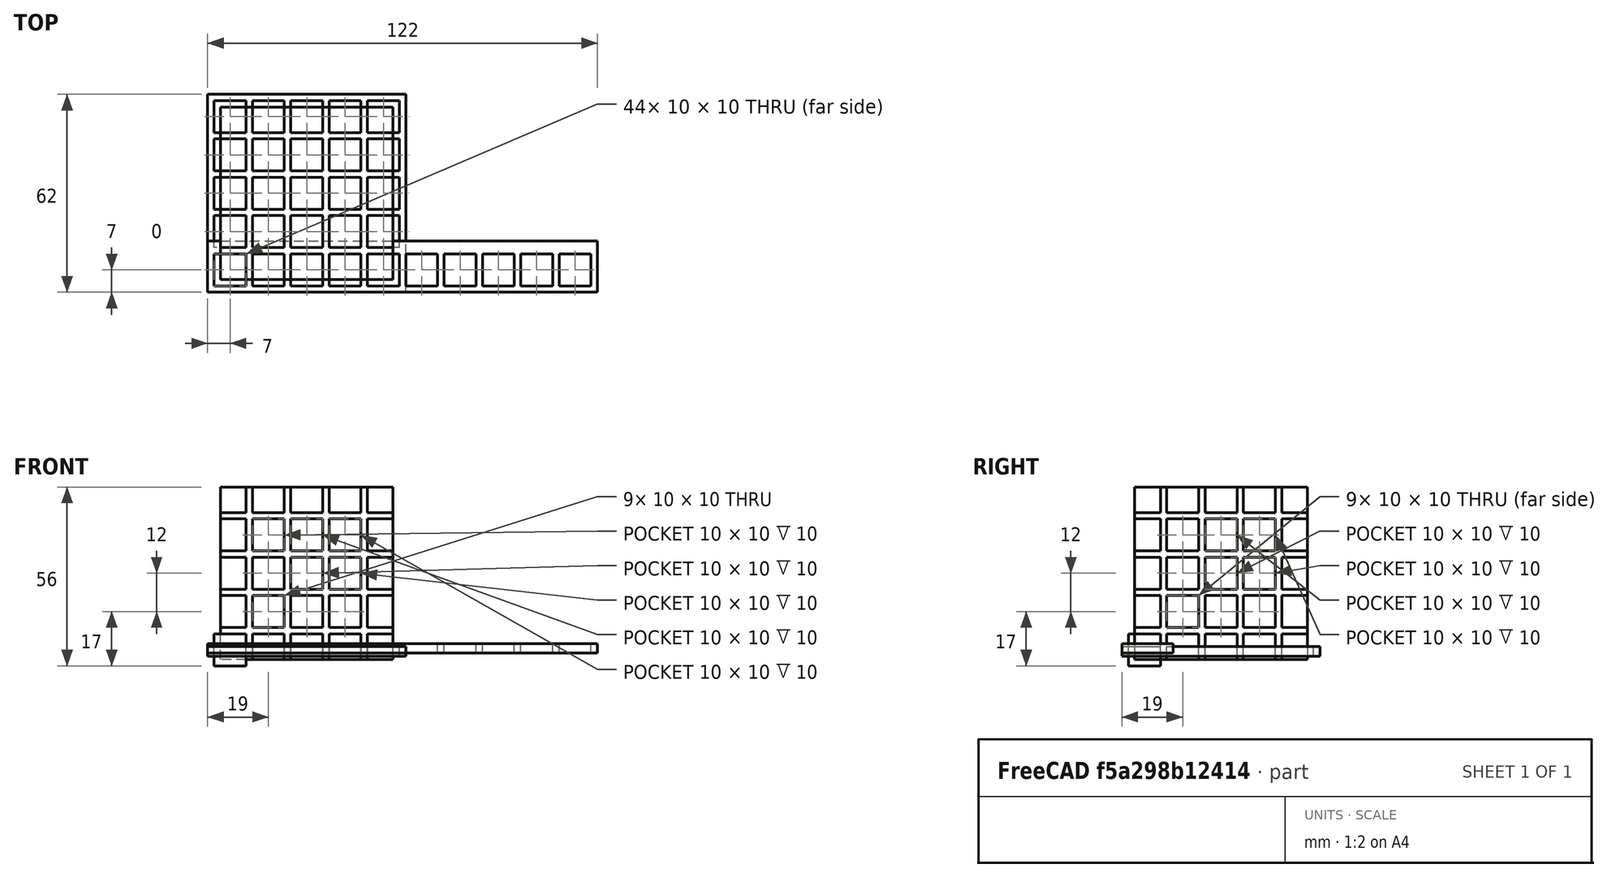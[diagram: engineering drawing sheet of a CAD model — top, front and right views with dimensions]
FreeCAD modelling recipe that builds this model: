
FCSTD DOCUMENT  (FreeCAD 1.0R39319 (Git))
Label: ojt1_t10p01_array
License: All rights reserved
LicenseURL: https://en.wikipedia.org/wiki/All_rights_reserved
objects: Part::Box×6, Part::FeaturePython×3, Part::Cut×3, PartDesign::Body×1
note: 10 computed .brp shape members not serialized (recipe doc carries the construction recipe); baked Part::Feature solids carry a one-line shape summary decoded from their .brp

FEATURE [PartDesign::Body] Body  label="master box"
  AllowCompound = false
  Origin = -> Origin
FEATURE [Part::Box] Box  label="Cub"
  AttacherType = Attacher::AttachEngine3D
  Height = 10
  Length = 10
  Width = 10
FEATURE [Part::FeaturePython] Array  # Draft array (typed FeaturePython)
  AlwaysSyncPlacement = false
  Angle = 360
  ArrayType = 0
  Axis = (0,0,1)
  Base = -> Box
  Center = (0,0,0)
  Count = 10
  ExpandArray = false
  Fuse = false
  IntervalAxis = (0,0,0)
  IntervalX = (12,0,0)
  IntervalY = (0,100,0)
  IntervalZ = (0,0,100)
  NumberCircles = 3
  NumberPolar = 5
  NumberX = 10
  NumberY = 1
  NumberZ = 1
  PlacementList = 10 placements: arithmetic series from (0,0,0) step (12,0,0) to (108,0,0)
  RadialDistance = 50
  ScaleList = (10) [(1,1,1),(1,1,1),(1,1,1),(1,1,1),(1,1,1),(1,1,1),(1,1,1),(1,1,1),(1,1,1),(1,1,1)]
  Symmetry = 1
  TangentialDistance = 25
FEATURE [Part::Box] Box001  label="Cub001"
  AttacherType = Attacher::AttachEngine3D
  Height = 3
  Length = 122
  Placement = pos=(-2,-2,4) rot=(0,0,1;0rad)
  Width = 16
FEATURE [Part::Cut] Cut
  Base = -> Box001
  Tool = -> Array
FEATURE [Part::Box] Box002  label="Cub002"
  AttacherType = Attacher::AttachEngine3D
  Height = 10
  Length = 10
  Width = 10
FEATURE [Part::FeaturePython] Array001  # Draft array (typed FeaturePython)
  AlwaysSyncPlacement = false
  Angle = 360
  ArrayType = 0
  Axis = (0,0,1)
  Base = -> Box002
  Center = (0,0,0)
  Count = 25
  ExpandArray = false
  Fuse = false
  IntervalAxis = (0,0,0)
  IntervalX = (12,0,0)
  IntervalY = (0,12,0)
  IntervalZ = (0,0,100)
  NumberCircles = 3
  NumberPolar = 5
  NumberX = 5
  NumberY = 5
  NumberZ = 1
  PlacementList = 25 placements: [(0,0,0),(0,12,0),(0,24,0),(0,36,0),(0,48,0),(12,0,0),(12,12,0),(12,24,0),(12,36,0),(12,48,0),(24,0,0),(24,12,0),(24,24,0),(24,36,0),(24,48,0),(36,0,0),(36,12,0),(36,24,0),(36,36,0),(36,48,0),(48,0,0),(48,12,0),(48,24,0),(48,36,0),(48,48,0)]
  RadialDistance = 50
  ScaleList = (25) [(1,1,1),(1,1,1),(1,1,1),(1,1,1),(1,1,1),(1,1,1),(1,1,1),(1,1,1),(1,1,1),(1,1,1),(1,1,1),(1,1,1),(1,1,1),(1,1,1),(1,1,1),(1,1,1),(1,1,1),(1,1,1),+7 more]
  Symmetry = 1
  TangentialDistance = 25
FEATURE [Part::Box] Box003  label="Cub003"
  AttacherType = Attacher::AttachEngine3D
  Height = 3
  Length = 62
  Placement = pos=(-2,-2,3) rot=(0,0,1;0rad)
  Width = 62
FEATURE [Part::Cut] Cut001
  Base = -> Box003
  Tool = -> Array001
FEATURE [Part::Box] Box004  label="Cub004"
  AttacherType = Attacher::AttachEngine3D
  Height = 10
  Length = 10
  Width = 10
FEATURE [Part::FeaturePython] Array002  # Draft array (typed FeaturePython)
  AlwaysSyncPlacement = false
  Angle = 360
  ArrayType = 0
  Axis = (0,0,1)
  Base = -> Box004
  Center = (0,0,0)
  Count = 125
  ExpandArray = false
  Fuse = false
  IntervalAxis = (0,0,0)
  IntervalX = (12,0,0)
  IntervalY = (0,12,0)
  IntervalZ = (0,0,12)
  NumberCircles = 3
  NumberPolar = 5
  NumberX = 5
  NumberY = 5
  NumberZ = 5
  PlacementList = 125 placements: [(0,0,0),(0,0,12),(0,0,24),(0,0,36),(0,0,48),(0,12,0),(0,12,12),(0,12,24),(0,12,36),(0,12,48),(0,24,0),(0,24,12),(0,24,24),(0,24,36),(0,24,48),(0,36,0),(0,36,12),(0,36,24),(0,36,36),(0,36,48),(0,48,0),(0,48,12),(0,48,24),(0,48,36),(0,48,48),(12,0,0),(12,0,12),(12,0,24),(12,0,36),(12,0,48),(12,12,0),(12,12,12),(12,12,24),(12,12,36),(12,12,48),(12,24,0),(12,24,12),(12,24,24),(12,24,36),(12,24,48),+85 more]
  RadialDistance = 50
  Symmetry = 1
  TangentialDistance = 25
FEATURE [Part::Box] Box005  label="Cub005"
  AttacherType = Attacher::AttachEngine3D
  Height = 54
  Length = 54
  Placement = pos=(2,2,2) rot=(0,0,1;0rad)
  Width = 54
FEATURE [Part::Cut] Cut002
  Base = -> Box005
  Tool = -> Array002
